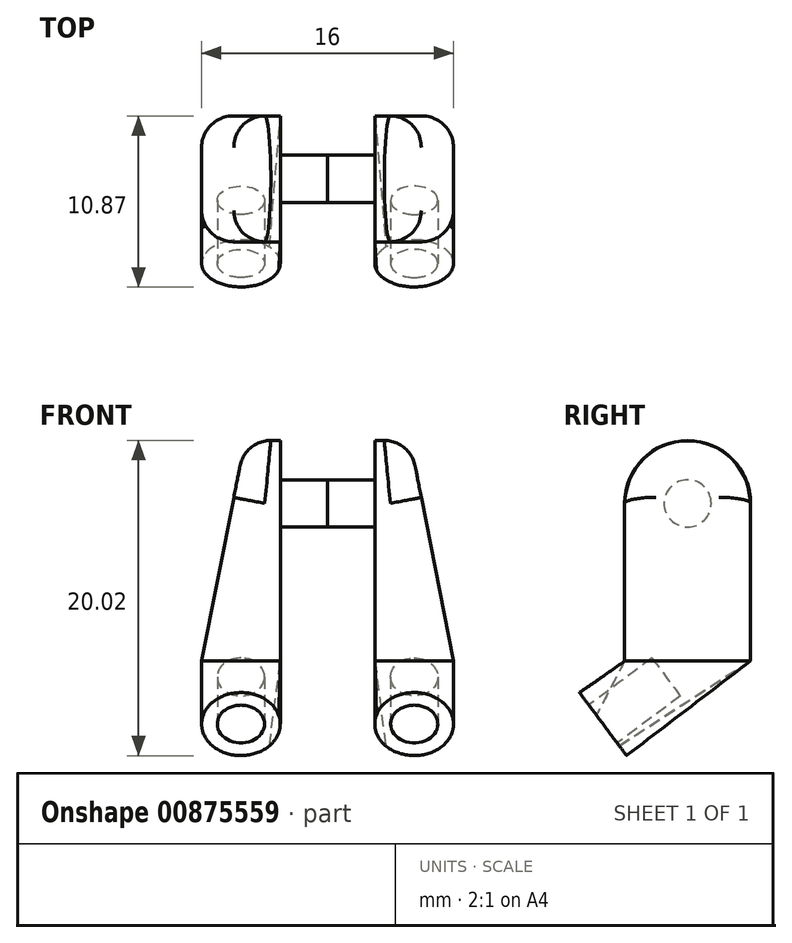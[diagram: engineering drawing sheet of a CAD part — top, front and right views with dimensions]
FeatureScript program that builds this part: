
annotation { "Feature Type Name" : "Feature", "Feature Type Description" : "" }
export const myFeature = defineFeature(function(context is Context, id is Id, definition is map)
    precondition{}
    {
        {
            var Q0;
            Q0=qCreatedBy(makeId("Right.planeOp"),FACE);
            var sketch = newSketch(context, id + "F0", { "sketchPlane" : qUnion([Q0])});
            skCircle(sketch, "E0", {"center": v(0, 0) * mm, "radius": 1.5 * mm});
            skSolve(sketch);
        }
        {
            var Q0;
            Q0=makeQuery(id+"F0.imprint","IMPRINT",FACE,{"disambiguationData":[TD([[makeQuery(id+"F0.imprint","IMPRINT",EDGE,{"derivedFrom":sQuery(id+"F0.wireOp",EDGE,"E0")}),1.0]])]});
            extrude(context, id + "F1", {"entities" : qUnion([Q0]), "depth" : 3 * mm, "offsetDistance" : 25 * mm});
        }
        {
            var Q0;
            Q0=makeQuery(id+"F1.opExtrude","CAP_FACE",FACE,{"disambiguationData":[OSD([sQuery(id+"F0.wireOp",EDGE,"E0")])],"isStart":false});
            var sketch = newSketch(context, id + "F2", { "sketchPlane" : qUnion([Q0])});
            skCircle(sketch, "E1", {"center": v(0, 0) * mm, "radius": 4 * mm});
            skLineSegment(sketch, "E2.bottom", {"start": v(4, 0) * mm, "end": v(-4, 0) * mm});
            skLineSegment(sketch, "E2.top", {"start": v(4, -10) * mm, "end": v(-4, -10) * mm});
            skLineSegment(sketch, "E2.left", {"start": v(4, 0) * mm, "end": v(4, -10) * mm});
            skLineSegment(sketch, "E2.right", {"start": v(-4, 0) * mm, "end": v(-4, -10) * mm});
            skPoint(sketch, "E2.middle", {"position": v(0, -5) * mm});
            skLineSegment(sketch, "E3", {"start": v(4, -10) * mm, "end": v(-3.94, -15.93) * mm, "construction": true});
            skLineSegment(sketch, "E4", {"start": v(-3.94, -15.93) * mm, "end": v(-6.8, -12.1) * mm, "construction": true});
            skLineSegment(sketch, "E5", {"start": v(-6.8, -12.1) * mm, "end": v(-4, -10) * mm, "construction": true});
            skLineSegment(sketch, "E6", {"start": v(-5.4, -14.01) * mm, "end": v(-3.65, -12.7) * mm, "construction": true});
            skPoint(sketch, "E6.startSnap0", {"position": v(-5.37, -14.01) * mm});
            skPoint(sketch, "E6.startSnap1", {"position": v(-5.4, -11.05) * mm});
            skSolve(sketch);
        }
        {
            var Q0;
            Q0 = qSketchRegion(id + "F2", true);
            extrude(context, id + "F3", {"entities" : qUnion([Q0]), "operationType" : NewBodyOperationType.ADD, "depth" : 5 * mm, "offsetDistance" : 25 * mm});
        }
        {
            var Q0;
            Q0=makeQuery(id+"F3.opExtrude","SWEPT_FACE",FACE,{"disambiguationData":[OSD([sQuery(id+"F2.wireOp",EDGE,"E2.right")])]});
            var sketch = newSketch(context, id + "F4", { "sketchPlane" : qUnion([Q0])});
            skLineSegment(sketch, "E7", {"start": v(8, -10) * mm, "end": v(4.97, 5.37) * mm});
            skLineSegment(sketch, "E8", {"start": v(4.97, 5.37) * mm, "end": v(10, 5.37) * mm});
            skLineSegment(sketch, "E9", {"start": v(10, 5.37) * mm, "end": v(8, -10) * mm});
            skSolve(sketch);
        }
        {
            var Q0;
            Q0 = qSketchRegion(id + "F4", true);
            extrude(context, id + "F5", {"entities" : qUnion([Q0]), "operationType" : NewBodyOperationType.REMOVE, "oppositeDirection" : true, "depth" : 25 * mm, "offsetDistance" : 25 * mm});
        }
        {
            var Q0;
            Q0=makeQuery(id+"F5.boolean.opBoolean","INTERSECT",EDGE,{"derivedFrom":[makeQuery(id+"F3.opExtrude","SWEPT_FACE",FACE,{"disambiguationData":[OSD([sQuery(id+"F2.wireOp",EDGE,"E1")])]}),makeQuery(id+"F5.opExtrude","SWEPT_FACE",FACE,{"disambiguationData":[OSD([sQuery(id+"F4.wireOp",EDGE,"E7")])]})]});
            var Q1;
            Q1=makeQuery(id+"F5.boolean.opBoolean","INTERSECT",EDGE,{"derivedFrom":[makeQuery(id+"F3.opExtrude","SWEPT_FACE",FACE,{"disambiguationData":[OSD([sQuery(id+"F2.wireOp",EDGE,"E2.left")])]}),makeQuery(id+"F5.opExtrude","SWEPT_FACE",FACE,{"disambiguationData":[OSD([sQuery(id+"F4.wireOp",EDGE,"E7")])]})]});
            fillet(context, id + "F6", {"entities" : qUnion([Q0, Q1]), "radius" : 2 * mm, "tangentPropagation" : true, "allowEdgeOverflow" : false});
        }
        {
            var Q0;
            Q0=sQuery(id+"F2.wireOp",VERTEX,"E4.end");
            var Q1;
            Q1=sQuery(id+"F2.wireOp",EDGE,"E5");
            cPlane(context, id + "F7", {"entities" : qUnion([Q0, Q1]), "cplaneType" : CPlaneType.LINE_POINT, "offset" : 25 * mm, "width" : 150 * mm, "height" : 150 * mm});
        }
        {
            var Q0;
            Q0=qCreatedBy(id+"F7.planeOp",FACE);
            var sketch = newSketch(context, id + "F8", { "sketchPlane" : qUnion([Q0])});
            skCircle(sketch, "E10", {"center": v(-5.5, -8.01) * mm, "radius": 2.5 * mm});
            skLineSegment(sketch, "E11", {"start": v(-3, -8.01) * mm, "end": v(-8, -8.01) * mm, "construction": true});
            skSolve(sketch);
        }
        {
            var Q1;
            Q1=makeQuery(id+"F3.opExtrude","SWEPT_FACE",FACE,{"disambiguationData":[OSD([sQuery(id+"F2.wireOp",EDGE,"E2.top")])]});
            var Q2;
            Q2=makeQuery(id+"F8.imprint","IMPRINT",FACE,{"disambiguationData":[TD([[makeQuery(id+"F8.imprint","IMPRINT",EDGE,{"derivedFrom":sQuery(id+"F8.wireOp",EDGE,"E10")}),1.0]])]});
            loft(context, id + "F9", {"operationType" : NewBodyOperationType.ADD, "sheetProfilesArray" : [{ "sheetProfileEntities" : qUnion([Q1]) }, { "sheetProfileEntities" : qUnion([Q2]) }]});
        }
        {
            var Q0;
            Q0=makeQuery(id+"F8.imprint","IMPRINT",FACE,{"disambiguationData":[TD([[makeQuery(id+"F8.imprint","IMPRINT",EDGE,{"derivedFrom":sQuery(id+"F8.wireOp",EDGE,"E10")}),1.0]])]});
            var sketch = newSketch(context, id + "F10", { "sketchPlane" : qUnion([Q0])});
            skCircle(sketch, "E12", {"center": v(-5.5, -8.01) * mm, "radius": 1.5 * mm});
            skSolve(sketch);
        }
        {
            var Q0;
            Q0=makeQuery(id+"F10.imprint","IMPRINT",FACE,{"disambiguationData":[TD([[makeQuery(id+"F10.imprint","IMPRINT",EDGE,{"derivedFrom":sQuery(id+"F10.wireOp",EDGE,"E12")}),1.0]])]});
            var Q1;
            Q1=sQuery(id+"F10.wireOp",EDGE,"E12");
            extrude(context, id + "F11", {"entities" : qUnion([Q0]), "operationType" : NewBodyOperationType.REMOVE, "surfaceEntities" : qUnion([Q1]), "depth" : 5 * mm, "offsetDistance" : 25 * mm});
        }
        {
            var Q0;
            Q0=makeQuery(id+"F1.opExtrude","SWEPT_BODY",BODY,{"disambiguationData":[OSD([sQuery(id+"F0.wireOp",EDGE,"E0")])]});
            var Q1;
            Q1=makeQuery(id+"F1.opExtrude","CAP_FACE",FACE,{"disambiguationData":[OSD([sQuery(id+"F0.wireOp",EDGE,"E0")])],"isStart":true});
            mirror(context, id + "F12", {"entities" : qUnion([Q0]), "mirrorPlane" : qUnion([Q1])});
        }
    });
